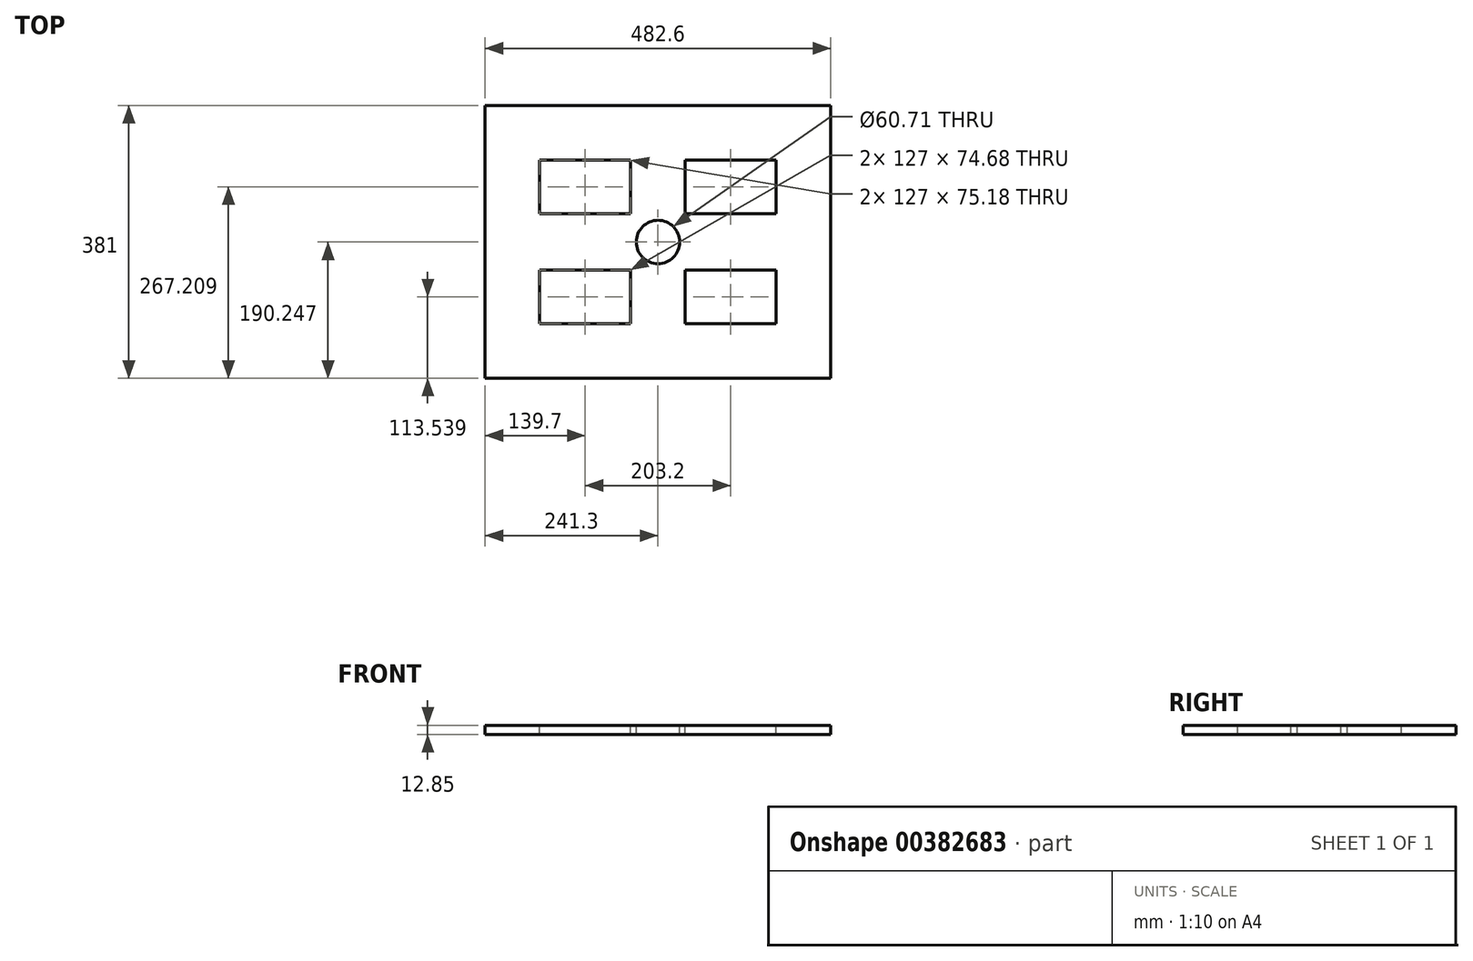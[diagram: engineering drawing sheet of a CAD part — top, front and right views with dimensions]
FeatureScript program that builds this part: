
annotation { "Feature Type Name" : "Feature", "Feature Type Description" : "" }
export const myFeature = defineFeature(function(context is Context, id is Id, definition is map)
    precondition{}
    {
        {
            var Q0;
            Q0=qCreatedBy(makeId("Top.planeOp"),FACE);
            var sketch = newSketch(context, id + "F0", { "sketchPlane" : qUnion([Q0])});
            skLineSegment(sketch, "E0.bottom", {"start": v(0, 0) * mm, "end": v(-482.6, 0) * mm});
            skLineSegment(sketch, "E0.top", {"start": v(0, -482.6) * mm, "end": v(-482.6, -482.6) * mm});
            skLineSegment(sketch, "E0.left", {"start": v(0, 0) * mm, "end": v(0, -482.6) * mm});
            skLineSegment(sketch, "E0.right", {"start": v(-482.6, 0) * mm, "end": v(-482.6, -482.6) * mm});
            skSolve(sketch);
        }
        {
            var Q0;
            Q0=makeQuery(id+"F0.imprint","IMPRINT",FACE,{"disambiguationData":[TD([[makeQuery(id+"F0.imprint","IMPRINT",EDGE,{"derivedFrom":sQuery(id+"F0.wireOp",EDGE,"E0.bottom")}),1.0]])]});
            extrude(context, id + "F1", {"entities" : qUnion([Q0]), "depth" : 12.85 * mm});
        }
        {
            var Q0;
            Q0=makeQuery(id+"F1.opExtrude","SWEPT_FACE",FACE,{"disambiguationData":[OSD([sQuery(id+"F0.wireOp",EDGE,"E0.top")])]});
            var sketch = newSketch(context, id + "F2", { "sketchPlane" : qUnion([Q0])});
            skLineSegment(sketch, "E1.bottom", {"start": v(0, 0) * mm, "end": v(-76.2, 0) * mm});
            skLineSegment(sketch, "E1.top", {"start": v(0, 12.85) * mm, "end": v(-76.2, 12.85) * mm});
            skLineSegment(sketch, "E1.left", {"start": v(0, 0) * mm, "end": v(0, 12.85) * mm});
            skLineSegment(sketch, "E1.right", {"start": v(-76.2, 0) * mm, "end": v(-76.2, 12.85) * mm});
            skLineSegment(sketch, "E2.bottom", {"start": v(-482.6, 12.85) * mm, "end": v(-406.4, 12.85) * mm});
            skLineSegment(sketch, "E2.top", {"start": v(-482.6, 0) * mm, "end": v(-406.4, 0) * mm});
            skLineSegment(sketch, "E2.left", {"start": v(-482.6, 12.85) * mm, "end": v(-482.6, 0) * mm});
            skLineSegment(sketch, "E2.right", {"start": v(-406.4, 12.85) * mm, "end": v(-406.4, 0) * mm});
            skSolve(sketch);
        }
        {
            var Q0;
            {var subQ0=sQuery(id+"F2.wireOp",EDGE,"E1.right");Q0=makeQuery(id+"F2.imprint","IMPRINT",FACE,{"disambiguationData":[TD([[makeQuery(id+"F2.imprint","IMPRINT",EDGE,{"derivedFrom":subQ0}),1.0]])]});}
            var Q1;
            Q1=makeQuery(id+"F2.imprint","IMPRINT",FACE,{"disambiguationData":[TD([[makeQuery(id+"F2.imprint","IMPRINT",EDGE,{"derivedFrom":sQuery(id+"F2.wireOp",EDGE,"E2.bottom")}),1.0]])]});
            extrude(context, id + "F3", {"entities" : qUnion([Q0, Q1]), "operationType" : NewBodyOperationType.REMOVE, "oppositeDirection" : true, "depth" : 50.8 * mm});
        }
        {
            var Q0;
            Q0=makeQuery(id+"F1.opExtrude","SWEPT_FACE",FACE,{"disambiguationData":[OSD([sQuery(id+"F0.wireOp",EDGE,"E0.bottom")])]});
            var sketch = newSketch(context, id + "F4", { "sketchPlane" : qUnion([Q0])});
            skLineSegment(sketch, "E3.bottom", {"start": v(0, 12.85) * mm, "end": v(76.2, 12.85) * mm});
            skLineSegment(sketch, "E3.top", {"start": v(0, 0) * mm, "end": v(76.2, 0) * mm});
            skLineSegment(sketch, "E3.left", {"start": v(0, 12.85) * mm, "end": v(0, 0) * mm});
            skLineSegment(sketch, "E3.right", {"start": v(76.2, 12.85) * mm, "end": v(76.2, 0) * mm});
            skLineSegment(sketch, "E4.bottom", {"start": v(482.6, 12.85) * mm, "end": v(406.4, 12.85) * mm});
            skLineSegment(sketch, "E4.top", {"start": v(482.6, 0) * mm, "end": v(406.4, 0) * mm});
            skLineSegment(sketch, "E4.left", {"start": v(482.6, 12.85) * mm, "end": v(482.6, 0) * mm});
            skLineSegment(sketch, "E4.right", {"start": v(406.4, 12.85) * mm, "end": v(406.4, 0) * mm});
            skSolve(sketch);
        }
        {
            var Q0;
            {var subQ0=sQuery(id+"F4.wireOp",EDGE,"E3.right");Q0=makeQuery(id+"F4.imprint","IMPRINT",FACE,{"disambiguationData":[TD([[makeQuery(id+"F4.imprint","IMPRINT",EDGE,{"derivedFrom":subQ0}),1.0]])]});}
            var Q1;
            Q1=makeQuery(id+"F4.imprint","IMPRINT",FACE,{"disambiguationData":[TD([[makeQuery(id+"F4.imprint","IMPRINT",EDGE,{"derivedFrom":sQuery(id+"F4.wireOp",EDGE,"E3.bottom")}),-1.0]])]});
            extrude(context, id + "F5", {"entities" : qUnion([Q0, Q1]), "operationType" : NewBodyOperationType.REMOVE, "oppositeDirection" : true, "depth" : 50.8 * mm});
        }
        {
            var Q0;
            Q0=makeQuery(id+"F1.opExtrude","CAP_FACE",FACE,{"disambiguationData":[OSD([sQuery(id+"F0.wireOp",EDGE,"E0.bottom"),sQuery(id+"F0.wireOp",EDGE,"E0.top"),sQuery(id+"F0.wireOp",EDGE,"E0.left"),sQuery(id+"F0.wireOp",EDGE,"E0.right")])],"isStart":false});
            var sketch = newSketch(context, id + "F6", { "sketchPlane" : qUnion([Q0])});
            skLineSegment(sketch, "E5.bottom", {"start": v(-406.4, -431.8) * mm, "end": v(-76.2, -431.8) * mm, "construction": true});
            skLineSegment(sketch, "E5.top", {"start": v(-406.4, -355.6) * mm, "end": v(-76.2, -355.6) * mm, "construction": true});
            skLineSegment(sketch, "E5.left", {"start": v(-406.4, -431.8) * mm, "end": v(-406.4, -355.6) * mm, "construction": true});
            skLineSegment(sketch, "E5.right", {"start": v(-76.2, -431.8) * mm, "end": v(-76.2, -355.6) * mm, "construction": true});
            skSolve(sketch);
        }
        {
            var Q0;
            {var subQ0=sQuery(id+"F0.wireOp",EDGE,"E0.top");Q0=makeQuery(id+"F6.imprint","IMPRINT",FACE,{"disambiguationData":[TD([[makeQuery(id+"F6.imprint","IMPRINT",EDGE,{"derivedFrom":makeQuery(id+"F1.opExtrude","CAP_EDGE",EDGE,{"disambiguationData":[OSD([subQ0])],"isStart":false})}),-1.0]])]});}
            var sketch = newSketch(context, id + "F7", { "sketchPlane" : qUnion([Q0])});
            skLineSegment(sketch, "E6.0.0", {"start": v(0, -482.6) * mm, "end": v(0, -50.8) * mm});
            skLineSegment(sketch, "E6.0.1", {"start": v(0, -50.8) * mm, "end": v(-406.4, -50.8) * mm});
            skLineSegment(sketch, "E6.0.2", {"start": v(-406.4, -50.8) * mm, "end": v(-406.4, 0) * mm});
            skLineSegment(sketch, "E6.0.3", {"start": v(-406.4, 0) * mm, "end": v(-482.6, 0) * mm});
            skLineSegment(sketch, "E6.0.4", {"start": v(-482.6, 0) * mm, "end": v(-482.6, -431.8) * mm});
            skLineSegment(sketch, "E6.0.5", {"start": v(-482.6, -431.8) * mm, "end": v(-76.2, -431.8) * mm});
            skLineSegment(sketch, "E6.0.6", {"start": v(-76.2, -431.8) * mm, "end": v(-76.2, -482.6) * mm});
            skLineSegment(sketch, "E6.0.7", {"start": v(-76.2, -482.6) * mm, "end": v(0, -482.6) * mm});
            skLineSegment(sketch, "E7.bottom", {"start": v(-406.4, -50.8) * mm, "end": v(-76.2, -50.8) * mm});
            skLineSegment(sketch, "E7.top", {"start": v(-406.4, -127) * mm, "end": v(-76.2, -127) * mm});
            skLineSegment(sketch, "E7.left", {"start": v(-406.4, -50.8) * mm, "end": v(-406.4, -127) * mm});
            skLineSegment(sketch, "E7.right", {"start": v(-76.2, -50.8) * mm, "end": v(-76.2, -127) * mm});
            skLineSegment(sketch, "E8.0", {"start": v(-406.4, -355.6) * mm, "end": v(-76.2, -355.6) * mm});
            skSolve(sketch);
        }
        {
            var Q0;
            {var subQ0=sQuery(id+"F0.wireOp",EDGE,"E0.top");Q0=makeQuery(id+"F6.imprint","IMPRINT",FACE,{"disambiguationData":[TD([[makeQuery(id+"F6.imprint","IMPRINT",EDGE,{"derivedFrom":makeQuery(id+"F1.opExtrude","CAP_EDGE",EDGE,{"disambiguationData":[OSD([subQ0])],"isStart":false})}),-1.0]])]});}
            var sketch = newSketch(context, id + "F8", { "sketchPlane" : qUnion([Q0])});
            skLineSegment(sketch, "E9.0", {"start": v(-406.4, -355.6) * mm, "end": v(-76.2, -355.6) * mm});
            skLineSegment(sketch, "E10.0", {"start": v(-406.4, -127) * mm, "end": v(-76.2, -127) * mm});
            skLineSegment(sketch, "E11.bottom", {"start": v(-279.4, -355.6) * mm, "end": v(-203.2, -355.6) * mm});
            skLineSegment(sketch, "E11.left", {"start": v(-279.4, -355.6) * mm, "end": v(-279.4, -280.92) * mm});
            skLineSegment(sketch, "E11.right", {"start": v(-203.2, -355.6) * mm, "end": v(-203.2, -280.92) * mm});
            skLineSegment(sketch, "E12.bottom", {"start": v(-279.4, -127) * mm, "end": v(-203.2, -127) * mm});
            skLineSegment(sketch, "E12.top", {"start": v(-279.4, -202.18) * mm, "end": v(-203.2, -202.18) * mm});
            skLineSegment(sketch, "E12.left", {"start": v(-279.4, -127) * mm, "end": v(-279.4, -202.18) * mm});
            skLineSegment(sketch, "E12.right", {"start": v(-203.2, -127) * mm, "end": v(-203.2, -202.18) * mm});
            skLineSegment(sketch, "E13.0.0", {"start": v(0, -482.6) * mm, "end": v(0, -50.8) * mm});
            skLineSegment(sketch, "E13.0.1", {"start": v(0, -50.8) * mm, "end": v(-406.4, -50.8) * mm});
            skLineSegment(sketch, "E13.0.2", {"start": v(-406.4, -50.8) * mm, "end": v(-406.4, 0) * mm});
            skLineSegment(sketch, "E13.0.3", {"start": v(-406.4, 0) * mm, "end": v(-482.6, 0) * mm});
            skLineSegment(sketch, "E13.0.4", {"start": v(-482.6, 0) * mm, "end": v(-482.6, -431.8) * mm});
            skLineSegment(sketch, "E13.0.5", {"start": v(-482.6, -431.8) * mm, "end": v(-76.2, -431.8) * mm});
            skLineSegment(sketch, "E13.0.6", {"start": v(-76.2, -431.8) * mm, "end": v(-76.2, -482.6) * mm});
            skLineSegment(sketch, "E13.0.7", {"start": v(-76.2, -482.6) * mm, "end": v(0, -482.6) * mm});
            skLineSegment(sketch, "E14.0", {"start": v(-406.4, -50.8) * mm, "end": v(-406.4, -127) * mm});
            skLineSegment(sketch, "E15", {"start": v(-406.4, -50.8) * mm, "end": v(-406.4, -431.8) * mm});
            skPoint(sketch, "E16.0", {"position": v(-76.2, -88.9) * mm});
            skLineSegment(sketch, "E17.0", {"start": v(-76.2, -50.8) * mm, "end": v(-76.2, -127) * mm});
            skLineSegment(sketch, "E18", {"start": v(-76.2, -50.8) * mm, "end": v(-76.2, -431.8) * mm});
            skLineSegment(sketch, "E19.left", {"start": v(-406.4, -202.18) * mm, "end": v(-406.4, -280.92) * mm});
            skLineSegment(sketch, "E19.right", {"start": v(-76.2, -202.18) * mm, "end": v(-76.2, -280.92) * mm});
            skLineSegment(sketch, "E20", {"start": v(-279.4, -280.92) * mm, "end": v(-406.4, -280.92) * mm});
            skLineSegment(sketch, "E21", {"start": v(-279.4, -280.92) * mm, "end": v(-76.2, -280.92) * mm});
            skLineSegment(sketch, "E22", {"start": v(-76.2, -202.18) * mm, "end": v(-406.4, -202.18) * mm});
            skSolve(sketch);
        }
        {
            var Q0;
            Q0=makeQuery(id+"F7.imprint","IMPRINT",FACE,{"disambiguationData":[TD([[makeQuery(id+"F7.imprint","IMPRINT",EDGE,{"derivedFrom":sQuery(id+"F7.wireOp",EDGE,"E7.top")}),-1.0]])]});
            var sketch = newSketch(context, id + "F9", { "sketchPlane" : qUnion([Q0])});
            skLineSegment(sketch, "E23.0", {"start": v(-279.4, -355.6) * mm, "end": v(-279.4, -280.92) * mm});
            skLineSegment(sketch, "E24.0", {"start": v(-279.4, -280.92) * mm, "end": v(-406.4, -280.92) * mm});
            skLineSegment(sketch, "E25.0", {"start": v(-406.4, -50.8) * mm, "end": v(-406.4, -431.8) * mm});
            skLineSegment(sketch, "E26.0", {"start": v(-406.4, -355.6) * mm, "end": v(-76.2, -355.6) * mm});
            skLineSegment(sketch, "E27.top", {"start": v(-279.4, -355.6) * mm, "end": v(-406.4, -355.6) * mm});
            skLineSegment(sketch, "E27.left", {"start": v(-279.4, -280.92) * mm, "end": v(-279.4, -355.6) * mm});
            skLineSegment(sketch, "E27.right", {"start": v(-406.4, -280.92) * mm, "end": v(-406.4, -355.6) * mm});
            skLineSegment(sketch, "E28.0", {"start": v(-279.4, -280.92) * mm, "end": v(-76.2, -280.92) * mm});
            skPoint(sketch, "E29.0", {"position": v(-203.2, -318.26) * mm});
            skLineSegment(sketch, "E30.0", {"start": v(-203.2, -355.6) * mm, "end": v(-203.2, -280.92) * mm});
            skLineSegment(sketch, "E31.0", {"start": v(-76.2, -50.8) * mm, "end": v(-76.2, -431.8) * mm});
            skLineSegment(sketch, "E32.bottom", {"start": v(-76.2, -280.92) * mm, "end": v(-203.2, -280.92) * mm});
            skLineSegment(sketch, "E32.top", {"start": v(-76.2, -355.6) * mm, "end": v(-203.2, -355.6) * mm});
            skLineSegment(sketch, "E32.left", {"start": v(-76.2, -280.92) * mm, "end": v(-76.2, -355.6) * mm});
            skLineSegment(sketch, "E32.right", {"start": v(-203.2, -280.92) * mm, "end": v(-203.2, -355.6) * mm});
            skSolve(sketch);
        }
        {
            var Q0;
            {var subQ3=sQuery(id+"F8.wireOp",EDGE,"E11.right");Q0=makeQuery(id+"F8.imprint","IMPRINT",FACE,{"disambiguationData":[TD([[makeQuery(id+"F8.imprint","IMPRINT",EDGE,{"derivedFrom":subQ3}),-1.0]])]});}
            var Q1;
            Q1=makeQuery(id+"F9.imprint","IMPRINT",FACE,{"disambiguationData":[TD([[makeQuery(id+"F9.imprint","IMPRINT",EDGE,{"derivedFrom":sQuery(id+"F9.wireOp",EDGE,"E24.0")}),1.0]])]});
            var Q2;
            {var subQ3=sQuery(id+"F8.wireOp",EDGE,"E12.left");Q2=makeQuery(id+"F8.imprint","IMPRINT",FACE,{"disambiguationData":[TD([[makeQuery(id+"F8.imprint","IMPRINT",EDGE,{"derivedFrom":subQ3}),-1.0]])]});}
            var Q3;
            {var subQ3=sQuery(id+"F8.wireOp",EDGE,"E12.right");Q3=makeQuery(id+"F8.imprint","IMPRINT",FACE,{"disambiguationData":[TD([[makeQuery(id+"F8.imprint","IMPRINT",EDGE,{"derivedFrom":subQ3}),1.0]])]});}
            extrude(context, id + "F10", {"entities" : qUnion([Q0, Q1, Q2, Q3]), "operationType" : NewBodyOperationType.REMOVE, "oppositeDirection" : true, "depth" : 25.4 * mm});
        }
        {
            var Q0;
            {var subQ0=sQuery(id+"F0.wireOp",EDGE,"E0.top");Q0=makeQuery(id+"F6.imprint","IMPRINT",FACE,{"disambiguationData":[TD([[makeQuery(id+"F6.imprint","IMPRINT",EDGE,{"derivedFrom":makeQuery(id+"F1.opExtrude","CAP_EDGE",EDGE,{"disambiguationData":[OSD([subQ0])],"isStart":false})}),-1.0]])]});}
            var sketch = newSketch(context, id + "F11", { "sketchPlane" : qUnion([Q0])});
            skCircle(sketch, "E33.0", {"center": v(-241.3, -241.55) * mm, "radius": 25.6 * mm});
            skCircle(sketch, "E34", {"center": v(-241.3, -241.55) * mm, "radius": 30.35 * mm});
            skSolve(sketch);
        }
        {
            var Q0;
            Q0=makeQuery(id+"F1.opExtrude","SWEPT_FACE",FACE,{"disambiguationData":[OSD([sQuery(id+"F0.wireOp",EDGE,"E0.top")])]});
            extrude(context, id + "F12", {"entities" : qUnion([Q0]), "operationType" : NewBodyOperationType.REMOVE, "oppositeDirection" : true, "depth" : 50.8 * mm});
        }
        {
            var Q0;
            Q0=makeQuery(id+"F1.opExtrude","SWEPT_FACE",FACE,{"disambiguationData":[OSD([sQuery(id+"F0.wireOp",EDGE,"E0.bottom")])]});
            extrude(context, id + "F13", {"entities" : qUnion([Q0]), "operationType" : NewBodyOperationType.REMOVE, "oppositeDirection" : true, "depth" : 50.8 * mm});
        }
        {
            var Q0;
            Q0=makeQuery(id+"F11.imprint","IMPRINT",FACE,{"disambiguationData":[TD([[makeQuery(id+"F11.imprint","IMPRINT",EDGE,{"derivedFrom":sQuery(id+"F11.wireOp",EDGE,"E34")}),-1.0]])]});
            var sketch = newSketch(context, id + "F14", { "sketchPlane" : qUnion([Q0])});
            skCircle(sketch, "E35.0", {"center": v(-241.3, -241.55) * mm, "radius": 30.35 * mm});
            skSolve(sketch);
        }
        {
            var Q0;
            Q0 = qSketchRegion(id + "F14", true);
            extrude(context, id + "F15", {"entities" : qUnion([Q0]), "operationType" : NewBodyOperationType.REMOVE, "oppositeDirection" : true, "depth" : 25.4 * mm});
        }
    });
